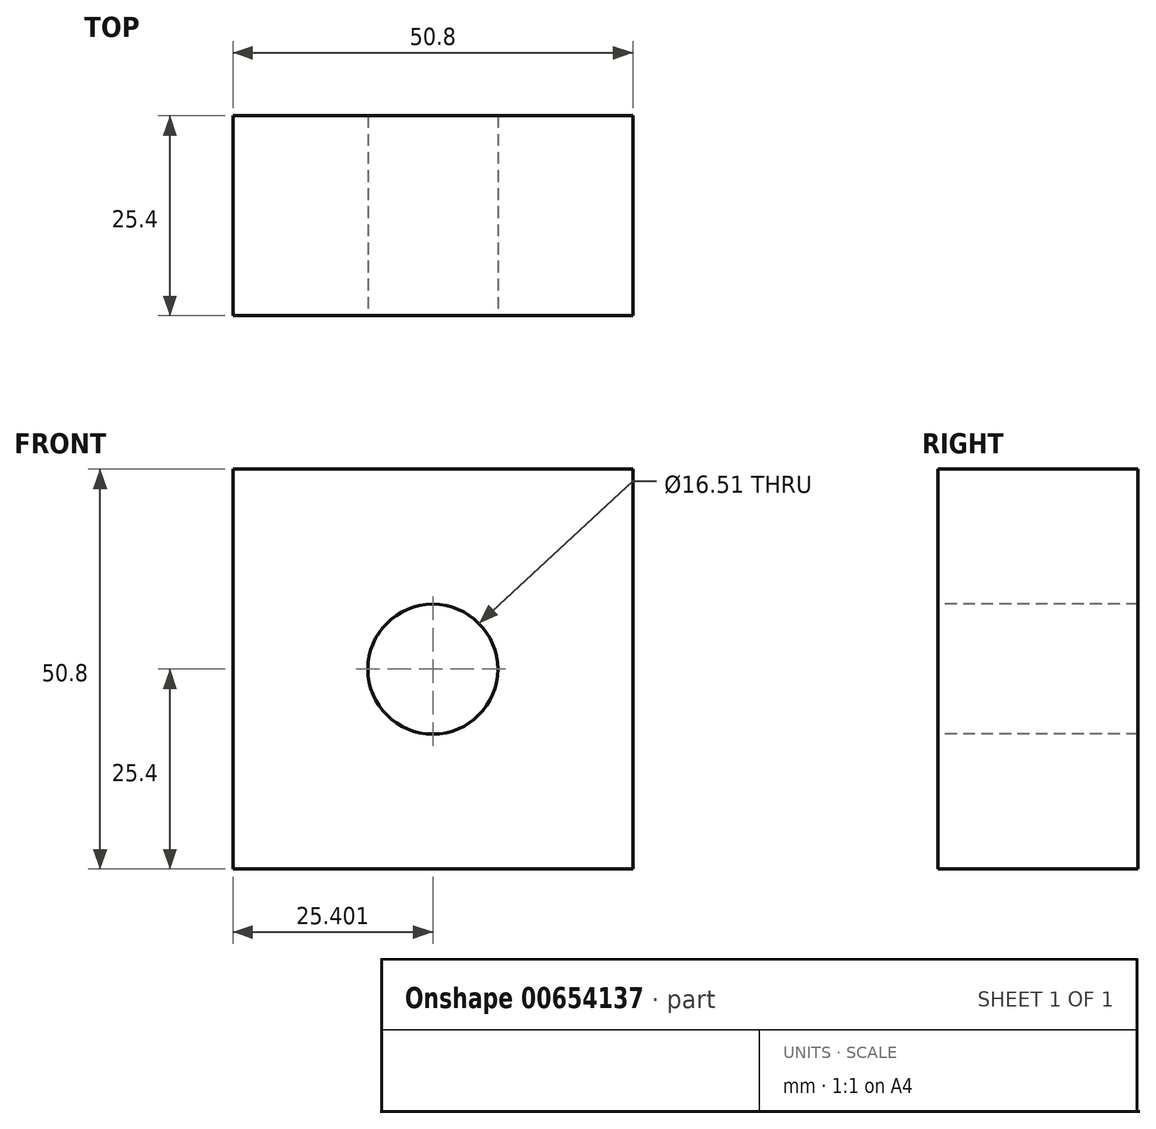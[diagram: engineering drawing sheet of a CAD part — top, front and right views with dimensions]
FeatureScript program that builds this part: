
annotation { "Feature Type Name" : "Feature", "Feature Type Description" : "" }
export const myFeature = defineFeature(function(context is Context, id is Id, definition is map)
    precondition{}
    {
        {
            var Q0;
            Q0=qCreatedBy(makeId("Front.planeOp"),FACE);
            var sketch = newSketch(context, id + "F0", { "sketchPlane" : qUnion([Q0])});
            skLineSegment(sketch, "E0", {"start": v(-47.09, 44.92) * mm, "end": v(3.71, 44.92) * mm});
            skLineSegment(sketch, "E1", {"start": v(3.71, 44.92) * mm, "end": v(3.71, -5.88) * mm});
            skLineSegment(sketch, "E2", {"start": v(3.71, -5.88) * mm, "end": v(-47.09, -5.88) * mm});
            skLineSegment(sketch, "E3", {"start": v(-47.09, -5.88) * mm, "end": v(-47.09, 44.92) * mm});
            skSolve(sketch);
        }
        {
            var Q0;
            Q0=qSketchRegion(id+"F0",true);
            extrude(context, id + "F1", {"entities" : qUnion([Q0]), "depth" : 25.4 * mm, "offsetDistance" : 25.4 * mm});
        }
        {
            var Q0;
            Q0=makeQuery(id+"F1.opExtrude","CAP_FACE",FACE,{"disambiguationData":[OSD([sQuery(id+"F0.wireOp",EDGE,"E0"),sQuery(id+"F0.wireOp",EDGE,"E1"),sQuery(id+"F0.wireOp",EDGE,"E2"),sQuery(id+"F0.wireOp",EDGE,"E3")])],"isStart":false});
            var sketch = newSketch(context, id + "F2", { "sketchPlane" : qUnion([Q0])});
            skCircle(sketch, "E4", {"center": v(-21.69, 19.52) * mm, "radius": 8.26 * mm});
            skSolve(sketch);
        }
        {
            var Q0;
            Q0=makeQuery(id+"F2.imprint","IMPRINT",FACE,{"disambiguationData":[TD([[makeQuery(id+"F2.imprint","IMPRINT",EDGE,{"derivedFrom":sQuery(id+"F2.wireOp",EDGE,"E4")}),1.0]])]});
            extrude(context, id + "F3", {"entities" : qUnion([Q0]), "operationType" : NewBodyOperationType.REMOVE, "endBound" : BoundingType.THROUGH_ALL, "oppositeDirection" : true, "depth" : 25.4 * mm, "offsetDistance" : 25.4 * mm});
        }
    });
